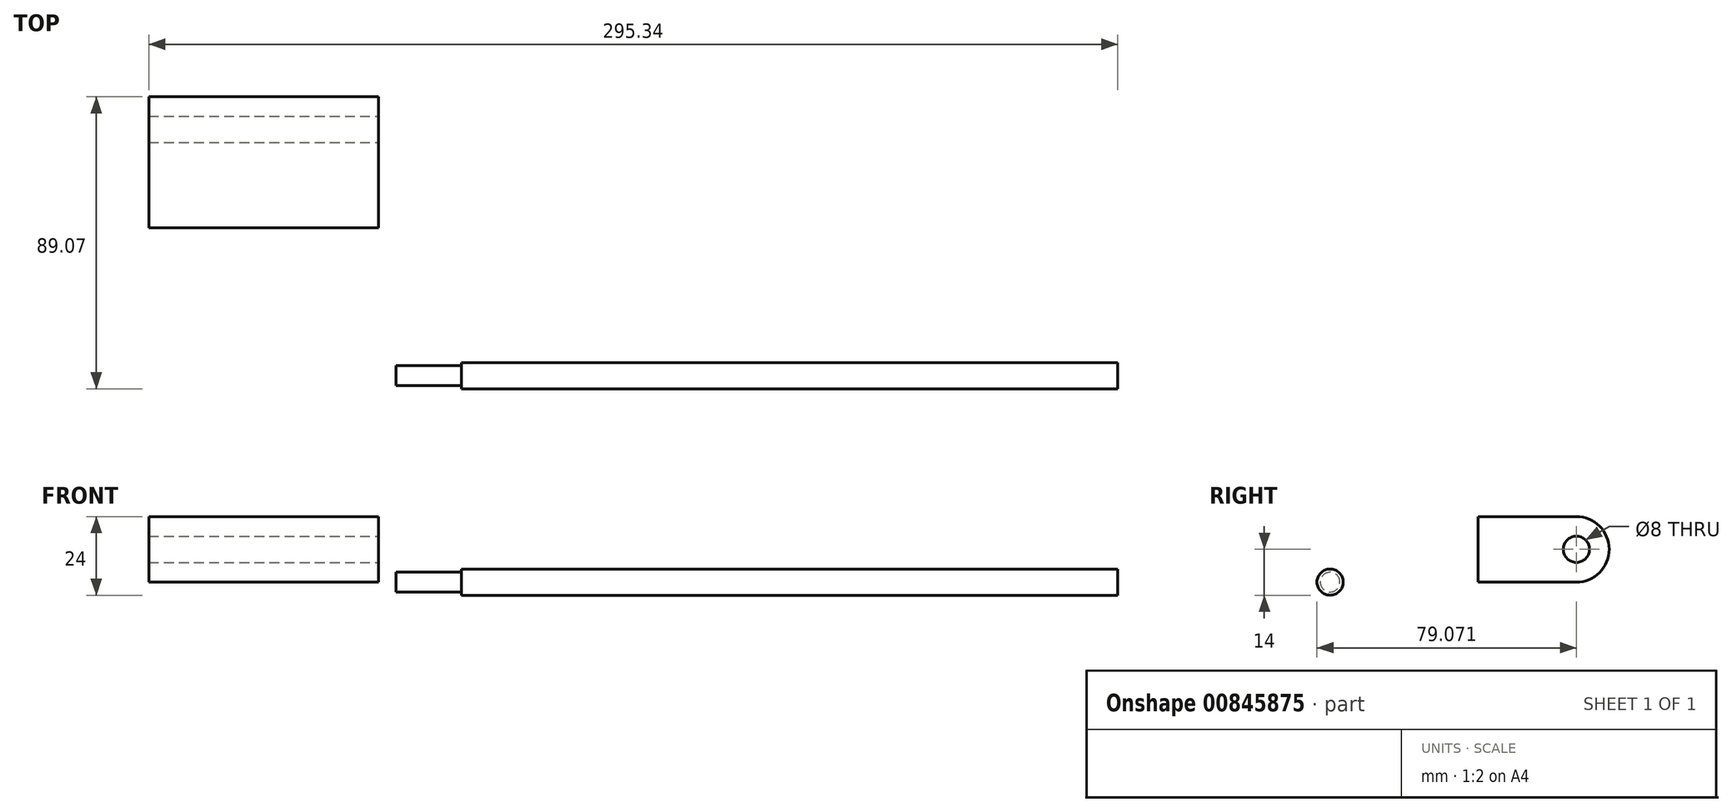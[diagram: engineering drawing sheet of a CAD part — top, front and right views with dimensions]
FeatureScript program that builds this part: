
annotation { "Feature Type Name" : "Feature", "Feature Type Description" : "" }
export const myFeature = defineFeature(function(context is Context, id is Id, definition is map)
    precondition{}
    {
        {
            var Q0;
            Q0=qCreatedBy(makeId("Right.planeOp"),FACE);
            var sketch = newSketch(context, id + "F0", { "sketchPlane" : qUnion([Q0])});
            skCircle(sketch, "E0", {"center": v(-69.33, 0) * mm, "radius": 4 * mm});
            skCircle(sketch, "E1", {"center": v(-69.33, 0) * mm, "radius": 3 * mm});
            skSolve(sketch);
        }
        {
            var Q0;
            Q0=makeQuery(id+"F0.imprint","IMPRINT",FACE,{"disambiguationData":[TD([[makeQuery(id+"F0.imprint","IMPRINT",EDGE,{"derivedFrom":sQuery(id+"F0.wireOp",EDGE,"E1")}),1.0]])]});
            extrude(context, id + "F1", {"entities" : qUnion([Q0]), "oppositeDirection" : true, "depth" : 20 * mm, "offsetDistance" : 25 * mm});
        }
        {
            var Q0;
            Q0=makeQuery(id+"F0.imprint","IMPRINT",FACE,{"disambiguationData":[TD([[makeQuery(id+"F0.imprint","IMPRINT",EDGE,{"derivedFrom":sQuery(id+"F0.wireOp",EDGE,"E0")}),1.0]])]});
            var Q1;
            Q1=makeQuery(id+"F1.opExtrude","CAP_FACE",FACE,{"disambiguationData":[OSD([sQuery(id+"F0.wireOp",EDGE,"E1")])],"isStart":true});
            extrude(context, id + "F2", {"entities" : qUnion([Q0, Q1]), "operationType" : NewBodyOperationType.ADD, "depth" : 200 * mm, "offsetDistance" : 25 * mm});
        }
        {
            var Q0;
            Q0=qCreatedBy(makeId("Top.planeOp"),FACE);
            var sketch = newSketch(context, id + "F3", { "sketchPlane" : qUnion([Q0])});
            skLineSegment(sketch, "E2.bottom", {"start": v(-95.34, 15.74) * mm, "end": v(-25.34, 15.74) * mm});
            skLineSegment(sketch, "E2.top", {"start": v(-95.34, -24.26) * mm, "end": v(-25.34, -24.26) * mm});
            skLineSegment(sketch, "E2.left", {"start": v(-95.34, 15.74) * mm, "end": v(-95.34, -24.26) * mm});
            skLineSegment(sketch, "E2.right", {"start": v(-25.34, 15.74) * mm, "end": v(-25.34, -24.26) * mm});
            skSolve(sketch);
        }
        {
            var Q0;
            Q0=makeQuery(id+"F3.imprint","IMPRINT",FACE,{"disambiguationData":[TD([[makeQuery(id+"F3.imprint","IMPRINT",EDGE,{"derivedFrom":sQuery(id+"F3.wireOp",EDGE,"E2.bottom")}),-1.0]])]});
            extrude(context, id + "F4", {"entities" : qUnion([Q0]), "depth" : 20 * mm, "offsetDistance" : 25 * mm});
        }
        {
            var Q0;
            Q0=makeQuery(id+"F4.opExtrude","CAP_EDGE",EDGE,{"disambiguationData":[OSD([sQuery(id+"F3.wireOp",EDGE,"E2.bottom")])],"isStart":false});
            var Q1;
            Q1=makeQuery(id+"F4.opExtrude","CAP_EDGE",EDGE,{"disambiguationData":[OSD([sQuery(id+"F3.wireOp",EDGE,"E2.bottom")])],"isStart":true});
            fillet(context, id + "F5", {"entities" : qUnion([Q0, Q1]), "radius" : 10 * mm, "tangentPropagation" : true, "allowEdgeOverflow" : false});
        }
        {
            var Q0;
            Q0=makeQuery(id+"F4.opExtrude","SWEPT_FACE",FACE,{"disambiguationData":[OSD([sQuery(id+"F3.wireOp",EDGE,"E2.right")])]});
            var sketch = newSketch(context, id + "F6", { "sketchPlane" : qUnion([Q0])});
            skCircle(sketch, "E3", {"center": v(5.74, 10) * mm, "radius": 4 * mm});
            skSolve(sketch);
        }
        {
            var Q0;
            Q0=makeQuery(id+"F6.imprint","IMPRINT",FACE,{"disambiguationData":[TD([[makeQuery(id+"F6.imprint","IMPRINT",EDGE,{"derivedFrom":sQuery(id+"F6.wireOp",EDGE,"E3")}),1.0]])]});
            extrude(context, id + "F7", {"entities" : qUnion([Q0]), "operationType" : NewBodyOperationType.REMOVE, "endBound" : BoundingType.THROUGH_ALL, "oppositeDirection" : true, "depth" : 25 * mm, "offsetDistance" : 25 * mm});
        }
    });
